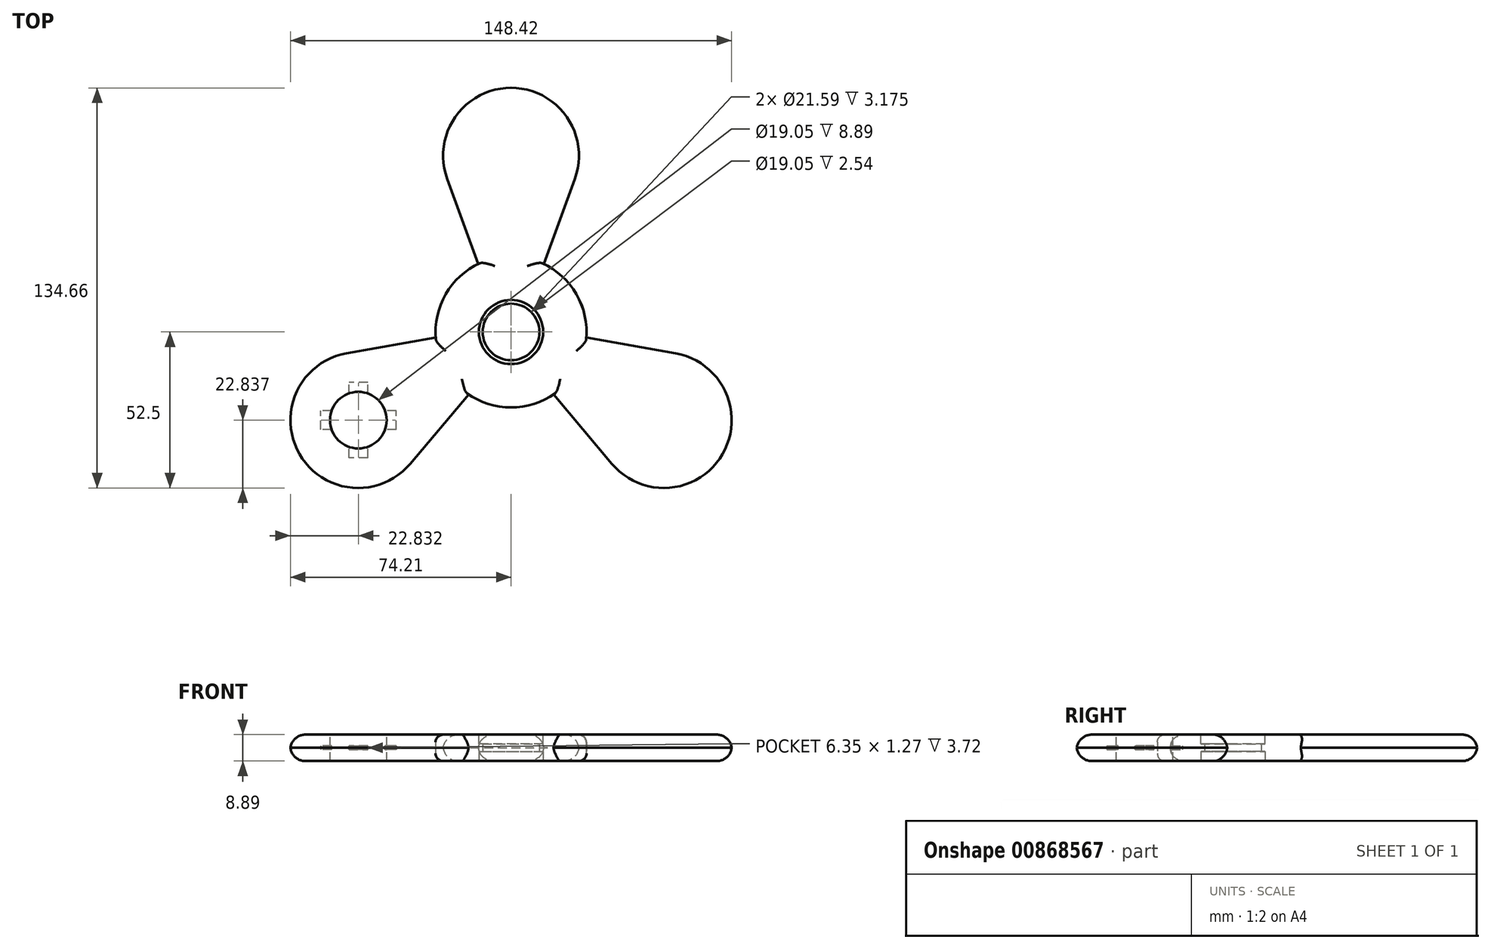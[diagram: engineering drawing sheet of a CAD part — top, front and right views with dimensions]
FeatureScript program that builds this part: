
annotation { "Feature Type Name" : "Feature", "Feature Type Description" : "" }
export const myFeature = defineFeature(function(context is Context, id is Id, definition is map)
    precondition{}
    {
        {
            var Q0;
            Q0=qCreatedBy(makeId("Top.planeOp"),FACE);
            var sketch = newSketch(context, id + "F0", { "sketchPlane" : qUnion([Q0])});
            skArc(sketch, "E0", {"start": v(-11.07, 22.86) * mm, "mid": v(-22, 12.7) * mm, "end": v(-25.33, -1.84) * mm});
            skLineSegment(sketch, "E1", {"start": v(0, 0) * mm, "end": v(0, 85.3) * mm, "construction": true});
            skLineSegment(sketch, "E2", {"start": v(0, 0) * mm, "end": v(73.9, -42.67) * mm, "construction": true});
            skLineSegment(sketch, "E3", {"start": v(0, 0) * mm, "end": v(-85.25, -49.22) * mm, "construction": true});
            skLineSegment(sketch, "E4", {"start": v(-11.07, 22.86) * mm, "end": v(-21.5, 51.5) * mm});
            skLineSegment(sketch, "E5", {"start": v(11.07, 22.86) * mm, "end": v(21.5, 51.5) * mm});
            skArc(sketch, "E6", {"start": v(21.5, 51.5) * mm, "mid": v(0, 82.2) * mm, "end": v(-21.5, 51.5) * mm});
            skArc(sketch, "E7.1.0", {"start": v(-55.35, -7.13) * mm, "mid": v(-71.19, -41.1) * mm, "end": v(-33.85, -44.37) * mm});
            skLineSegment(sketch, "E7.1.1", {"start": v(-25.33, -1.84) * mm, "end": v(-55.35, -7.13) * mm});
            skLineSegment(sketch, "E7.1.2", {"start": v(-14.26, -21.02) * mm, "end": v(-33.85, -44.37) * mm});
            skArc(sketch, "E7.2.0", {"start": v(33.85, -44.37) * mm, "mid": v(71.19, -41.1) * mm, "end": v(55.35, -7.13) * mm});
            skLineSegment(sketch, "E7.2.1", {"start": v(14.26, -21.02) * mm, "end": v(33.85, -44.37) * mm});
            skLineSegment(sketch, "E7.2.2", {"start": v(25.33, -1.84) * mm, "end": v(55.35, -7.13) * mm});
            skCircle(sketch, "E8", {"center": v(0, 0) * mm, "radius": 9.53 * mm});
            skArc(sketch, "E9.trimOffspring", {"start": v(25.33, -1.84) * mm, "mid": v(22, 12.7) * mm, "end": v(11.07, 22.86) * mm});
            skArc(sketch, "E10.trimOffspring", {"start": v(-14.26, -21.02) * mm, "mid": v(0, -25.4) * mm, "end": v(14.26, -21.02) * mm});
            skSolve(sketch);
        }
        {
            var Q0;
            Q0=qSketchRegion(id+"F0",true);
            extrude(context, id + "F1", {"entities" : qUnion([Q0]), "depth" : 8.9 * mm, "offsetDistance" : 25.4 * mm});
        }
        {
            var Q0;
            Q0=makeQuery(id+"F1.opExtrude","CAP_EDGE",EDGE,{"disambiguationData":[OSD([sQuery(id+"F0.wireOp",EDGE,"E7.1.0")])],"isStart":false});
            var Q1;
            Q1=makeQuery(id+"F1.opExtrude","CAP_EDGE",EDGE,{"disambiguationData":[OSD([sQuery(id+"F0.wireOp",EDGE,"E7.1.0")])],"isStart":true});
            var Q2;
            Q2=makeQuery(id+"F1.opExtrude","CAP_EDGE",EDGE,{"disambiguationData":[OSD([sQuery(id+"F0.wireOp",EDGE,"E6")])],"isStart":false});
            var Q3;
            Q3=makeQuery(id+"F1.opExtrude","CAP_EDGE",EDGE,{"disambiguationData":[OSD([sQuery(id+"F0.wireOp",EDGE,"E6")])],"isStart":true});
            var Q4;
            Q4=makeQuery(id+"F1.opExtrude","CAP_EDGE",EDGE,{"disambiguationData":[OSD([sQuery(id+"F0.wireOp",EDGE,"E7.2.0")])],"isStart":false});
            var Q5;
            Q5=makeQuery(id+"F1.opExtrude","CAP_EDGE",EDGE,{"disambiguationData":[OSD([sQuery(id+"F0.wireOp",EDGE,"E7.2.0")])],"isStart":true});
            fillet(context, id + "F2", {"entities" : qUnion([Q0, Q1, Q2, Q3, Q4, Q5]), "radius" : 5.08 * mm, "tangentPropagation" : true, "allowEdgeOverflow" : false});
        }
        {
            var Q0;
            Q0=makeQuery(id+"F1.opExtrude","CAP_EDGE",EDGE,{"disambiguationData":[OSD([sQuery(id+"F0.wireOp",EDGE,"E9.trimOffspring")])],"isStart":false});
            var Q1;
            Q1=makeQuery(id+"F1.opExtrude","CAP_EDGE",EDGE,{"disambiguationData":[OSD([sQuery(id+"F0.wireOp",EDGE,"E9.trimOffspring")])],"isStart":true});
            var Q2;
            Q2=makeQuery(id+"F1.opExtrude","CAP_EDGE",EDGE,{"disambiguationData":[OSD([sQuery(id+"F0.wireOp",EDGE,"E0")])],"isStart":true});
            var Q3;
            Q3=makeQuery(id+"F1.opExtrude","CAP_EDGE",EDGE,{"disambiguationData":[OSD([sQuery(id+"F0.wireOp",EDGE,"E10.trimOffspring")])],"isStart":true});
            var Q4;
            Q4=makeQuery(id+"F1.opExtrude","CAP_EDGE",EDGE,{"disambiguationData":[OSD([sQuery(id+"F0.wireOp",EDGE,"E10.trimOffspring")])],"isStart":false});
            var Q5;
            Q5=makeQuery(id+"F1.opExtrude","CAP_EDGE",EDGE,{"disambiguationData":[OSD([sQuery(id+"F0.wireOp",EDGE,"E0")])],"isStart":false});
            fillet(context, id + "F3", {"entities" : qUnion([Q0, Q1, Q2, Q3, Q4, Q5]), "radius" : 2.54 * mm, "tangentPropagation" : true, "allowEdgeOverflow" : false});
        }
        {
            var Q0;
            Q0=makeQuery(id+"F1.opExtrude","CAP_FACE",FACE,{"disambiguationData":[OSD([sQuery(id+"F0.wireOp",EDGE,"E0"),sQuery(id+"F0.wireOp",EDGE,"E4"),sQuery(id+"F0.wireOp",EDGE,"E5"),sQuery(id+"F0.wireOp",EDGE,"E6"),sQuery(id+"F0.wireOp",EDGE,"E7.1.0"),sQuery(id+"F0.wireOp",EDGE,"E7.1.1"),sQuery(id+"F0.wireOp",EDGE,"E7.1.2"),sQuery(id+"F0.wireOp",EDGE,"E7.2.0"),sQuery(id+"F0.wireOp",EDGE,"E7.2.1"),sQuery(id+"F0.wireOp",EDGE,"E7.2.2"),sQuery(id+"F0.wireOp",EDGE,"E8"),sQuery(id+"F0.wireOp",EDGE,"E9.trimOffspring"),sQuery(id+"F0.wireOp",EDGE,"E10.trimOffspring")])],"isStart":false});
            var sketch = newSketch(context, id + "F4", { "sketchPlane" : qUnion([Q0])});
            skCircle(sketch, "E11", {"center": v(0, 0) * mm, "radius": 10.8 * mm});
            skSolve(sketch);
        }
        {
            var Q0;
            Q0=qSketchRegion(id+"F4",true);
            extrude(context, id + "F5", {"entities" : qUnion([Q0]), "operationType" : NewBodyOperationType.REMOVE, "oppositeDirection" : true, "depth" : 3.17 * mm, "offsetDistance" : 25.4 * mm});
        }
        {
            var Q0;
            Q0=makeQuery(id+"F1.opExtrude","CAP_FACE",FACE,{"disambiguationData":[OSD([sQuery(id+"F0.wireOp",EDGE,"E0"),sQuery(id+"F0.wireOp",EDGE,"E4"),sQuery(id+"F0.wireOp",EDGE,"E5"),sQuery(id+"F0.wireOp",EDGE,"E6"),sQuery(id+"F0.wireOp",EDGE,"E7.1.0"),sQuery(id+"F0.wireOp",EDGE,"E7.1.1"),sQuery(id+"F0.wireOp",EDGE,"E7.1.2"),sQuery(id+"F0.wireOp",EDGE,"E7.2.0"),sQuery(id+"F0.wireOp",EDGE,"E7.2.1"),sQuery(id+"F0.wireOp",EDGE,"E7.2.2"),sQuery(id+"F0.wireOp",EDGE,"E8"),sQuery(id+"F0.wireOp",EDGE,"E9.trimOffspring"),sQuery(id+"F0.wireOp",EDGE,"E10.trimOffspring")])],"isStart":true});
            var sketch = newSketch(context, id + "F6", { "sketchPlane" : qUnion([Q0])});
            skCircle(sketch, "E12", {"center": v(0, 0) * mm, "radius": 10.8 * mm});
            skSolve(sketch);
        }
        {
            var Q0;
            Q0=qSketchRegion(id+"F6",true);
            extrude(context, id + "F7", {"entities" : qUnion([Q0]), "operationType" : NewBodyOperationType.REMOVE, "oppositeDirection" : true, "depth" : 3.17 * mm, "offsetDistance" : 25.4 * mm});
        }
        {
            var Q0;
            Q0=makeQuery(id+"F1.opExtrude","CAP_FACE",FACE,{"disambiguationData":[OSD([sQuery(id+"F0.wireOp",EDGE,"E0"),sQuery(id+"F0.wireOp",EDGE,"E4"),sQuery(id+"F0.wireOp",EDGE,"E5"),sQuery(id+"F0.wireOp",EDGE,"E6"),sQuery(id+"F0.wireOp",EDGE,"E7.1.0"),sQuery(id+"F0.wireOp",EDGE,"E7.1.1"),sQuery(id+"F0.wireOp",EDGE,"E7.1.2"),sQuery(id+"F0.wireOp",EDGE,"E7.2.0"),sQuery(id+"F0.wireOp",EDGE,"E7.2.1"),sQuery(id+"F0.wireOp",EDGE,"E7.2.2"),sQuery(id+"F0.wireOp",EDGE,"E8"),sQuery(id+"F0.wireOp",EDGE,"E9.trimOffspring"),sQuery(id+"F0.wireOp",EDGE,"E10.trimOffspring")])],"isStart":false});
            var sketch = newSketch(context, id + "F8", { "sketchPlane" : qUnion([Q0])});
            skCircle(sketch, "E13", {"center": v(-51.38, -29.66) * mm, "radius": 9.53 * mm});
            skSolve(sketch);
        }
        {
            var Q0;
            Q0=qSketchRegion(id+"F8",true);
            extrude(context, id + "F9", {"entities" : qUnion([Q0]), "operationType" : NewBodyOperationType.REMOVE, "endBound" : BoundingType.THROUGH_ALL, "oppositeDirection" : true, "depth" : 25.4 * mm, "offsetDistance" : 25.4 * mm});
        }
        {
            var Q0;
            Q0=makeQuery(id+"F1.opExtrude","CAP_FACE",FACE,{"disambiguationData":[OSD([sQuery(id+"F0.wireOp",EDGE,"E0"),sQuery(id+"F0.wireOp",EDGE,"E4"),sQuery(id+"F0.wireOp",EDGE,"E5"),sQuery(id+"F0.wireOp",EDGE,"E6"),sQuery(id+"F0.wireOp",EDGE,"E7.1.0"),sQuery(id+"F0.wireOp",EDGE,"E7.1.1"),sQuery(id+"F0.wireOp",EDGE,"E7.1.2"),sQuery(id+"F0.wireOp",EDGE,"E7.2.0"),sQuery(id+"F0.wireOp",EDGE,"E7.2.1"),sQuery(id+"F0.wireOp",EDGE,"E7.2.2"),sQuery(id+"F0.wireOp",EDGE,"E8"),sQuery(id+"F0.wireOp",EDGE,"E9.trimOffspring"),sQuery(id+"F0.wireOp",EDGE,"E10.trimOffspring")])],"isStart":true});
            cPlane(context, id + "F10", {"entities" : qUnion([Q0]), "cplaneType" : CPlaneType.OFFSET, "offset" : 4.44 * mm, "oppositeDirection" : true, "width" : 152.4 * mm, "height" : 152.4 * mm});
        }
        {
            var Q0;
            Q0=qCreatedBy(id+"F10.planeOp",FACE);
            var sketch = newSketch(context, id + "F11", { "sketchPlane" : qUnion([Q0])});
            skLineSegment(sketch, "E14", {"start": v(-41.85, 29.66) * mm, "end": v(-60.9, 29.66) * mm, "construction": true});
            skLineSegment(sketch, "E15", {"start": v(-51.38, 39.19) * mm, "end": v(-51.38, 20.14) * mm, "construction": true});
            skLineSegment(sketch, "E16.bottom", {"start": v(-38.68, 32.84) * mm, "end": v(-48.2, 32.84) * mm});
            skLineSegment(sketch, "E16.top", {"start": v(-38.68, 26.49) * mm, "end": v(-48.2, 26.49) * mm});
            skLineSegment(sketch, "E16.left", {"start": v(-38.68, 32.84) * mm, "end": v(-38.68, 26.49) * mm});
            skLineSegment(sketch, "E16.right", {"start": v(-64.08, 32.84) * mm, "end": v(-64.08, 26.49) * mm});
            skLineSegment(sketch, "E17.bottom", {"start": v(-48.2, 42.36) * mm, "end": v(-54.55, 42.36) * mm});
            skLineSegment(sketch, "E17.top", {"start": v(-48.2, 16.96) * mm, "end": v(-54.55, 16.96) * mm});
            skLineSegment(sketch, "E17.left", {"start": v(-48.2, 42.36) * mm, "end": v(-48.2, 32.84) * mm});
            skLineSegment(sketch, "E17.right", {"start": v(-54.55, 42.36) * mm, "end": v(-54.55, 32.84) * mm});
            skLineSegment(sketch, "E18.trimOffspring", {"start": v(-48.2, 26.49) * mm, "end": v(-48.2, 16.96) * mm});
            skLineSegment(sketch, "E19.trimOffspring", {"start": v(-54.55, 32.84) * mm, "end": v(-64.08, 32.84) * mm});
            skLineSegment(sketch, "E20.trimOffspring", {"start": v(-54.55, 26.49) * mm, "end": v(-54.55, 16.96) * mm});
            skLineSegment(sketch, "E21.trimOffspring", {"start": v(-54.55, 26.49) * mm, "end": v(-64.08, 26.49) * mm});
            skSolve(sketch);
        }
        {
            var Q0;
            Q0=qSketchRegion(id+"F11",true);
            extrude(context, id + "F12", {"entities" : qUnion([Q0]), "operationType" : NewBodyOperationType.REMOVE, "endBound" : BoundingType.SYMMETRIC, "oppositeDirection" : true, "depth" : 1.27 * mm, "offsetDistance" : 25.4 * mm});
        }
    });
